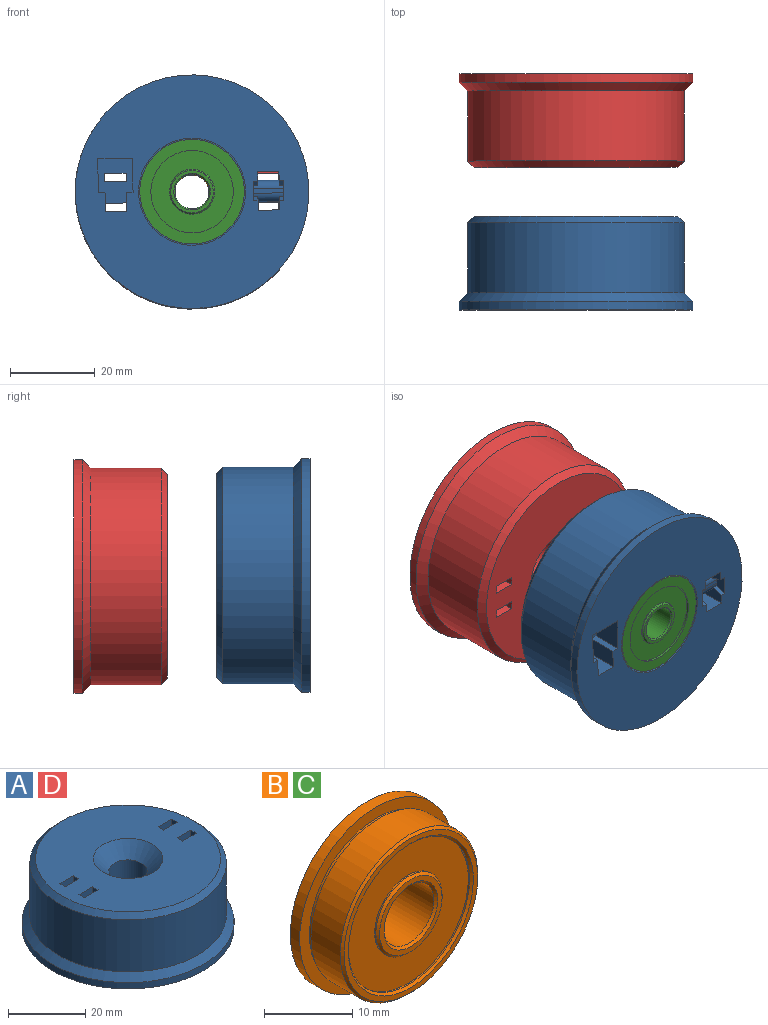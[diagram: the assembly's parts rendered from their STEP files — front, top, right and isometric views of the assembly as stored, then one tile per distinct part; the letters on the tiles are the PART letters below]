
ASSEMBLY  parts=4 mates=1
PART A: 43 faces, bbox 55x55x22 mm
  f0: plane 55x55mm, normal (0,0,-1), area 1733.8mm2, adj f5,f6,f8,f9,f10,f12,f14,f15
  f1: plane 14.8x2mm, normal (-1,0,0), area 29.6mm2, adj f2,f13,f18,f29
  f2: plane 14.8x5mm, normal (0,1,0), area 74mm2, adj f1,f3,f18,f29
  f3: plane 14.8x2mm, normal (1,0,0), area 29.6mm2, adj f2,f13,f18,f29
  f4: plane 17.5x5mm, normal (0,-1,0), area 87.5mm2, adj f5,f14,f18,f36
  f5: plane 22x3.16mm, normal (-1,0,0), area 46.4mm2, adj f0,f4,f6,f18,f36,f39
  f6: plane 22x5mm, normal (0,1,0), area 110mm2, adj f0,f5,f14,f18
  f7: plane 14.8x5mm, normal (0,-1,0), area 74mm2, adj f8,f15,f18,f29
  f8: plane 22x4.5mm, normal (-1,0,0), area 62mm2, adj f0,f7,f9,f18,f24,f29
  f9: plane 22x5mm, normal (0,1,0), area 110mm2, adj f0,f8,f15,f18
  f10: plane 22x3.16mm, normal (-1,0,0), area 46.4mm2, adj f0,f11,f16,f18,f35,f40
  f11: plane 17.5x5mm, normal (0,1,0), area 87.5mm2, adj f10,f12,f18,f35
  f12: plane 22x3.16mm, normal (1,0,0), area 46.4mm2, adj f0,f11,f16,f18,f35,f41
  f13: plane 14.8x5mm, normal (0,-1,0), area 74mm2, adj f1,f3,f18,f29
  f14: plane 22x3.16mm, normal (1,0,0), area 46.4mm2, adj f0,f4,f6,f18,f36,f42
  f15: plane 22x4.5mm, normal (1,0,0), area 62mm2, adj f0,f7,f9,f18,f28,f29
  f16: plane 22x5mm, normal (0,-1,0), area 110mm2, adj f0,f10,f12,f18
  f17: cylinder r=5mm len=10.9mm, axis (0,0,-1), area 342.4mm2, adj f22,f37
  f18: plane 48x48mm, normal (0,0,1), area 1515.1mm2, adj f1,f2,f3,f4,f5,f6,f7,f8
  f19: cylinder r=12.6mm len=25.2mm, axis (0,0,-1), area 126.7mm2, adj f0,f20
  f20: plane 25.2x25.2mm, normal (0,0,-1), area 115.2mm2, adj f19,f21
  f21: cylinder r=11.05mm len=22.1mm, axis (0,0,-1), area 381.9mm2, adj f20,f22
  f22: plane 22.1x22.1mm, normal (0,0,-1), area 305.1mm2, adj f17,f21
  f23: cylinder r=25.5mm len=51mm, axis (0,0,-1), area 2643.7mm2, adj f31,f38
  f24: plane 7.2x1.6mm, normal (0,1,0), area 11.5mm2, adj f0,f8,f25,f29
  f25: plane 8x7.2mm, normal (-1,0,0), area 57.6mm2, adj f0,f24,f26,f29
  f26: plane 8.2x7.2mm, normal (0,-1,0), area 59mm2, adj f0,f25,f27,f29
  f27: plane 8x7.2mm, normal (1,0,0), area 57.6mm2, adj f0,f26,f28,f29
  f28: plane 7.2x1.6mm, normal (0,1,0), area 11.5mm2, adj f0,f15,f27,f29
  f29: plane 10.5x8.2mm, normal (0,0,-1), area 68.1mm2, adj f1,f2,f3,f7,f8,f13,f15,f24
  f30: cylinder r=27.5mm len=55mm, axis (0,0,-1), area 345.6mm2, adj f0,f31
  f31: cone r=25.5mm half-angle=45deg, axis (0,0,-1), area 470.9mm2, adj f23,f30
  f32: plane 4.64x2.69mm, normal (-1,0,0), area 9.4mm2, adj f0,f34,f35,f36,f39,f40
  f33: plane 4.64x2.69mm, normal (1,0,0), area 9.4mm2, adj f0,f34,f35,f36,f41,f42
  f34: plane 7.2x1mm, normal (0,0,-1), area 7.2mm2, adj f32,f33,f35,f36
  f35: cylinder r=2mm len=7.2mm, axis (-1,0,0), area 17.6mm2, adj f10,f11,f12,f32,f33,f34,f40,f41
  f36: cylinder r=2mm len=7.2mm, axis (1,0,0), area 17.6mm2, adj f4,f5,f14,f32,f33,f34,f39,f42
  f37: cone r=5mm half-angle=45deg, axis (0,0,1), area 248.8mm2, adj f17,f18
  f38: cone r=24mm half-angle=45deg, axis (0,0,-1), area 329.9mm2, adj f18,f23
  f39: plane 2.69x1.1mm, normal (0,0.94,-0.34), area 3.1mm2, adj f0,f5,f32,f36
  f40: plane 2.69x1.1mm, normal (0,-0.94,-0.34), area 3.1mm2, adj f0,f10,f32,f35
  f41: plane 2.69x1.1mm, normal (0,-0.94,-0.34), area 3.1mm2, adj f0,f12,f33,f35
  f42: plane 2.69x1.1mm, normal (0,0.94,-0.34), area 3.1mm2, adj f0,f14,f33,f36
PART B: 22 faces, bbox 24.6x7x24.6 mm
  f0: cylinder r=9.7mm len=19.4mm, axis (0,1,0), area 12.2mm2, adj f1,f18
  f1: plane 19.4x19.4mm, normal (0,-1,0), area 207.3mm2, adj f0,f2
  f2: cylinder r=5.3mm len=10.6mm, axis (0,1,0), area 6.7mm2, adj f1,f20
  f3: plane 10x10mm, normal (0,-1,0), area 20.5mm2, adj f20,f21
  f4: cylinder r=4mm len=8mm, axis (0,1,0), area 160.8mm2, adj f17,f21
  f5: plane 10x10mm, normal (0,1,0), area 20.5mm2, adj f16,f17
  f6: cylinder r=5.3mm len=10.6mm, axis (0,1,0), area 6.7mm2, adj f7,f16
  f7: plane 19.4x19.4mm, normal (0,1,0), area 207.3mm2, adj f6,f8
  f8: cylinder r=9.7mm len=19.4mm, axis (0,1,0), area 30.5mm2, adj f7,f9
  f9: plane 24.6x24.6mm, normal (0,1,0), area 179.7mm2, adj f8,f10
  f10: cylinder r=12.3mm len=24.6mm, axis (0,1,0), area 115.9mm2, adj f9,f11
  f11: plane 24.6x24.6mm, normal (0,-1,0), area 112.2mm2, adj f10,f12
  f12: cylinder r=10.75mm len=21.5mm, axis (0,1,0), area 33.8mm2, adj f11,f13
  f13: plane 22x22mm, normal (0,1,0), area 17.1mm2, adj f12,f14
  f14: cylinder r=11mm len=22mm, axis (0,1,0), area 324.8mm2, adj f13,f19
  f15: plane 21.4x21.4mm, normal (0,-1,0), area 45.5mm2, adj f18,f19
  f16: cone r=5mm half-angle=45deg, axis (0,-1,0), area 13.7mm2, adj f5,f6
  f17: cone r=4mm half-angle=45deg, axis (0,1,0), area 11.1mm2, adj f4,f5
  f18: cone r=10mm half-angle=45deg, axis (0,-1,0), area 26.3mm2, adj f0,f15
  f19: cone r=11mm half-angle=45deg, axis (0,1,0), area 28.9mm2, adj f14,f15
  f20: cone r=5.3mm half-angle=45deg, axis (0,1,0), area 13.7mm2, adj f2,f3
  f21: cone r=4.3mm half-angle=45deg, axis (0,-1,0), area 11.1mm2, adj f3,f4
PART C: same geometry as B
PART D: same geometry as A
PLACE A rot(axis=(0,0.71,0.71),179.6deg) t=(19.03,-42.11,6.79)mm
PLACE B t=(18.98,9.55,6.63)mm
PLACE C rot(axis=(-0.01,0,1),180deg) t=(19.03,-38.51,6.79)mm
PLACE D rot(axis=(1,0,0),90deg) t=(18.98,13.45,6.63)mm
MATE slider A.f17 <-> C.f0  axis (0,-1,0) through (19.03,-35.01,6.79)mm
